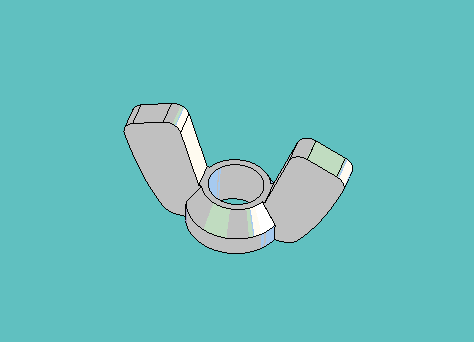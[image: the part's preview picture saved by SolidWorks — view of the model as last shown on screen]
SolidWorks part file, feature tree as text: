
SOLIDWORKS PART (.sldprt)
format: sldprt  version: not decoded by parser v0  size: 222,720 bytes
history: native  units: mm
features: sketch x3, extrude x2, material x1, chamfer x1, fillet x1 (+11 scaffold rows collapsed)
feature tree (19):
  scaffold x11  (default folders/planes/origin — collapsed)
  material  "Material <not specified>"
  sketch  "Sketch1"  dims[D1=6.35mm D2=11.1125mm]
  extrude  "Extrude1"  Depth=5.55625mm
  sketch  "Sketch2"  dims[D1=1.5875mm]
  chamfer  "Chamfer2"  Distance=3.175mm
  sketch  "Sketch3"  dims[D1=~10.31875mm D2=11.1125mm D3=~7.14375mm D4=0.508mm]
  extrude  "Extrude2"  Depth=1.5875mm
  fillet  "Fillet1"  Radius=1.5875mm
decode coverage: 7 of 7 modeling features carry decoded parameters
note: ~ marks probable driven/reference dimensions
note: suppression state not decoded; provenance and decode notes live in map.json
